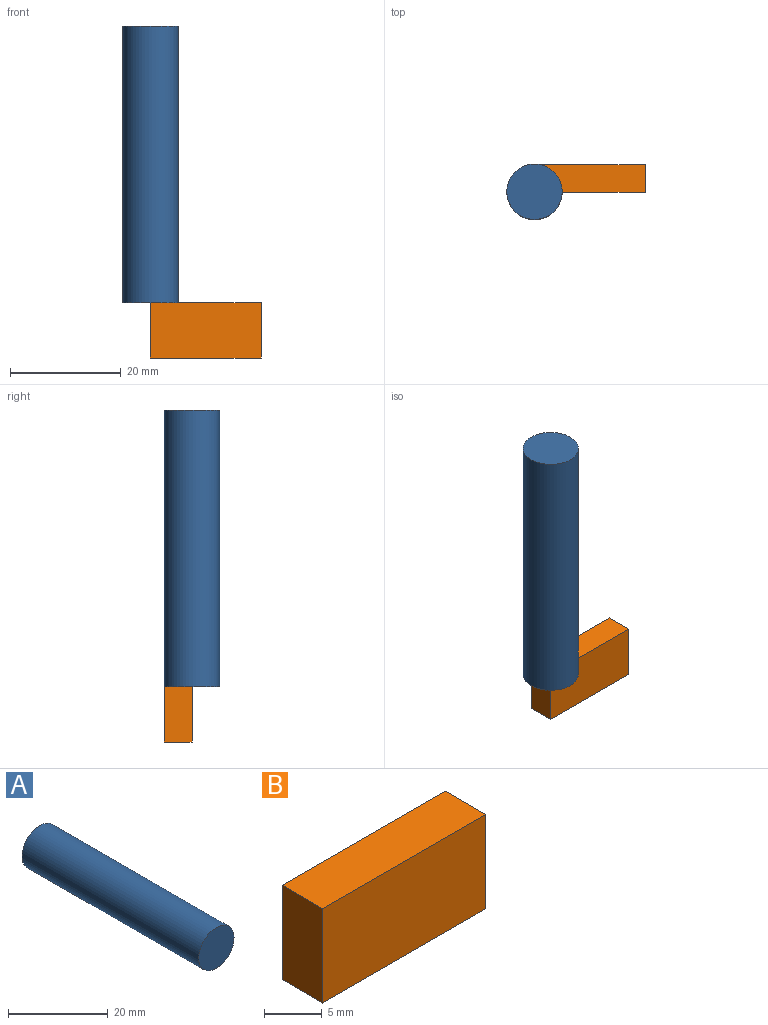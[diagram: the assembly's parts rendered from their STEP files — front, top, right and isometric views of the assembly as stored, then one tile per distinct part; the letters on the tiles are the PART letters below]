
ASSEMBLY  parts=2 mates=1
PART A: 3 faces, bbox 10x50x10 mm
  f0: cylinder r=5mm len=50mm, axis (0,1,0), area 1570.8mm2, adj f1,f2
  f1: plane 10x10mm, normal (0,1,0), area 78.5mm2, adj f0
  f2: plane 10x10mm, normal (0,-1,0), area 78.5mm2, adj f0
PART B: 6 faces, bbox 20x5x10 mm
  f0: plane 20x5mm, normal (0,0,1), area 100mm2, adj f1,f3,f4,f5
  f1: plane 10x5mm, normal (-1,0,0), area 50mm2, adj f0,f2,f4,f5
  f2: plane 20x5mm, normal (0,0,-1), area 100mm2, adj f1,f3,f4,f5
  f3: plane 10x5mm, normal (1,0,0), area 50mm2, adj f0,f2,f4,f5
  f4: plane 20x10mm, normal (0,-1,0), area 200mm2, adj f0,f1,f2,f3
  f5: plane 20x10mm, normal (0,1,0), area 200mm2, adj f0,f1,f2,f3
PLACE A rot(axis=(1,0,0),90deg) t=(-14.03,-3.72,26.66)mm
PLACE B t=(-4.03,1.28,-28.34)mm
MATE planar A.f0 <-> B.f0  axis (0,0,-1) through (-14.03,-3.72,-23.34)mm
